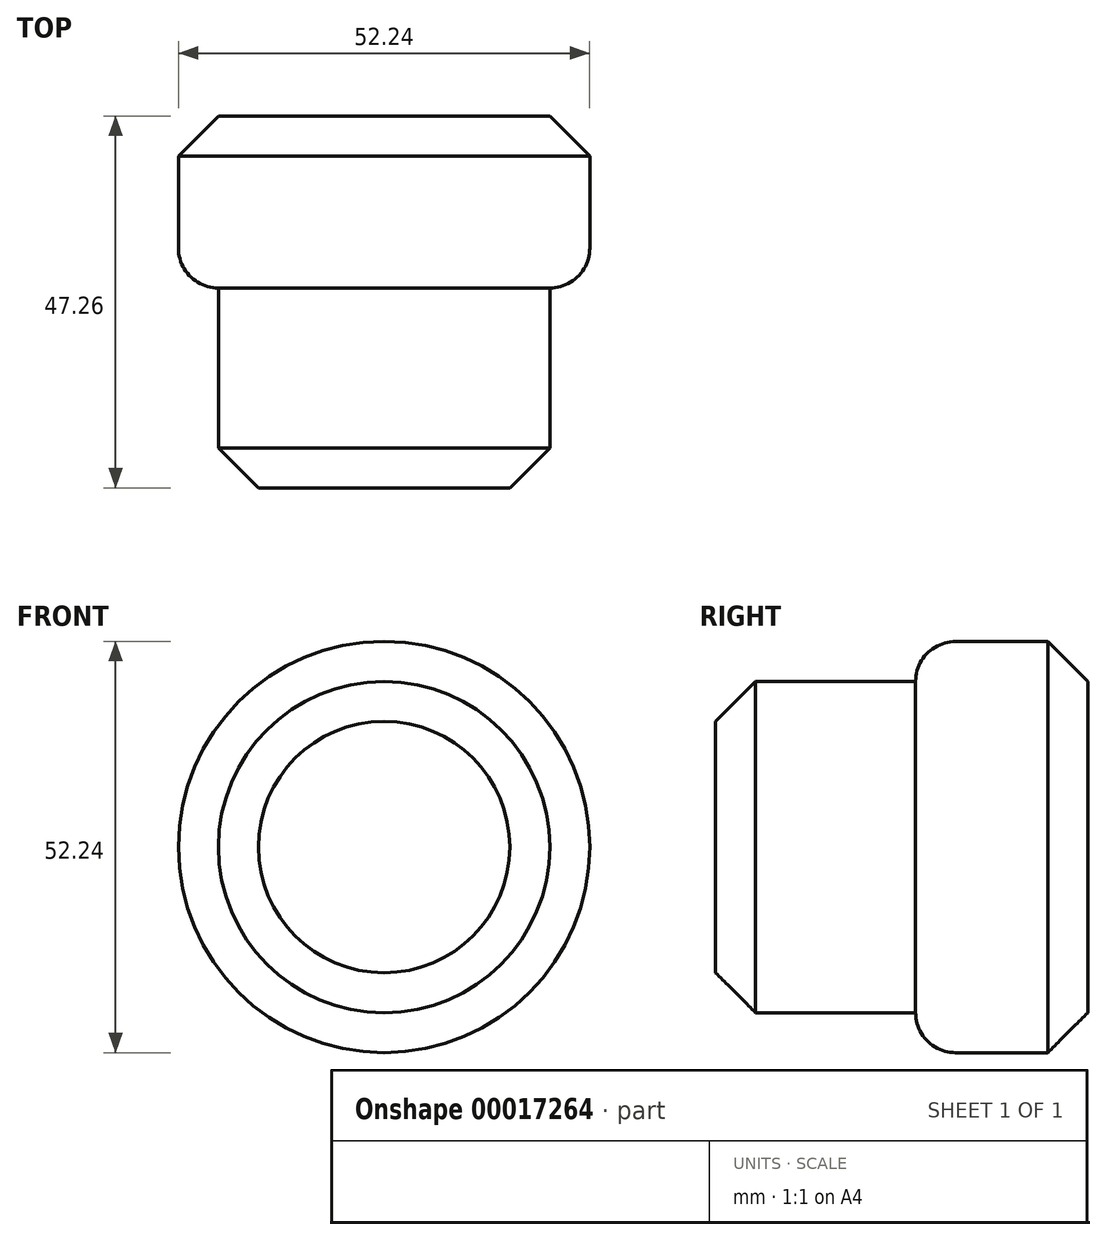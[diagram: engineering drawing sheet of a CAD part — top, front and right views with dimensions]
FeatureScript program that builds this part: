
annotation { "Feature Type Name" : "Feature", "Feature Type Description" : "" }
export const myFeature = defineFeature(function(context is Context, id is Id, definition is map)
    precondition{}
    {
        {
            var Q0;
            Q0=qCreatedBy(makeId("Front.planeOp"),FACE);
            var sketch = newSketch(context, id + "F0", { "sketchPlane" : qUnion([Q0])});
            skCircle(sketch, "E0", {"center": v(0, 0) * mm, "radius": 26.12 * mm});
            skSolve(sketch);
        }
        {
            var Q0;
            Q0=makeQuery(id+"F0.imprint","IMPRINT",FACE,{"disambiguationData":[TD([[makeQuery(id+"F0.imprint","IMPRINT",EDGE,{"derivedFrom":sQuery(id+"F0.wireOp",EDGE,"E0")}),1.0]])]});
            extrude(context, id + "F1", {"entities" : qUnion([Q0]), "depth" : 21.86 * mm});
        }
        {
            var Q0;
            Q0=makeQuery(id+"F1.opExtrude","CAP_EDGE",EDGE,{"disambiguationData":[OSD([sQuery(id+"F0.wireOp",EDGE,"E0")])],"isStart":false});
            fillet(context, id + "F3", {"entities" : qUnion([Q0]), "radius" : 5.08 * mm, "tangentPropagation" : true, "allowEdgeOverflow" : false});
        }
        {
            var Q0;
            Q0=makeQuery(id+"F1.opExtrude","CAP_EDGE",EDGE,{"disambiguationData":[OSD([sQuery(id+"F0.wireOp",EDGE,"E0")])],"isStart":true});
            chamfer(context, id + "F4", {"entities" : qUnion([Q0]), "width" : 5.08 * mm, "tangentPropagation" : true});
        }
        {
            var Q0;
            Q0=makeQuery(id+"F1.opExtrude","CAP_FACE",FACE,{"disambiguationData":[OSD([sQuery(id+"F0.wireOp",EDGE,"E0")])],"isStart":false});
            extrude(context, id + "F2", {"entities" : qUnion([Q0]), "operationType" : NewBodyOperationType.ADD, "depth" : 25.4 * mm});
        }
        {
            var Q0;
            Q0=makeQuery(id+"F2.opExtrude","CAP_EDGE",EDGE,{"disambiguationData":[OSD([sQuery(id+"F0.wireOp",EDGE,"E0")])],"isStart":false});
            chamfer(context, id + "F5", {"entities" : qUnion([Q0]), "width" : 5.08 * mm, "tangentPropagation" : true});
        }
    });
